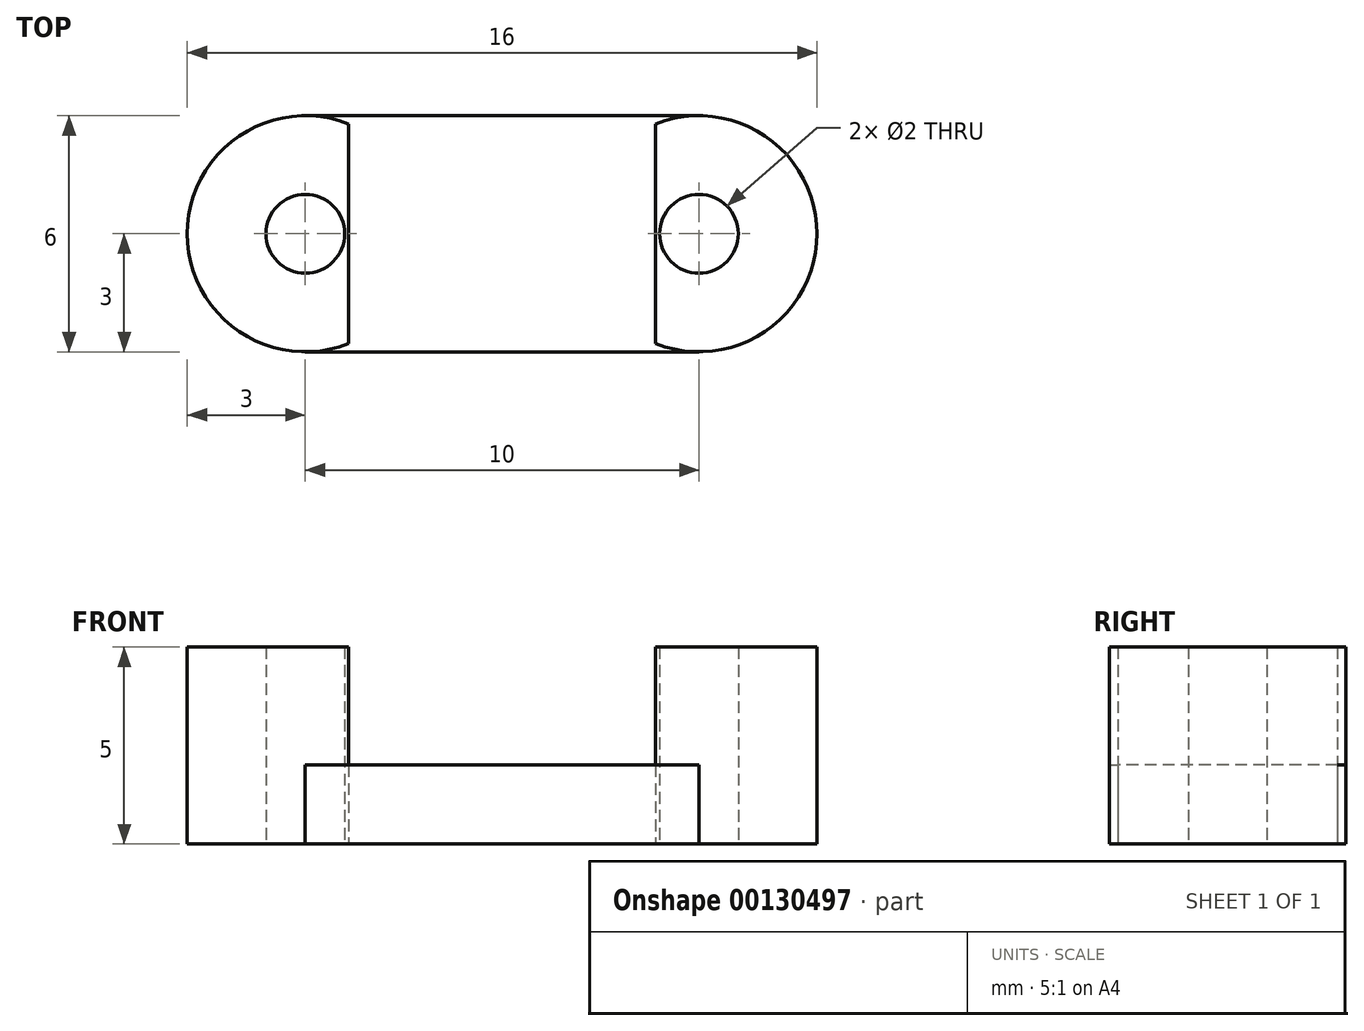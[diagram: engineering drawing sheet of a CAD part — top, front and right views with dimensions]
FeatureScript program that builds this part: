
annotation { "Feature Type Name" : "Feature", "Feature Type Description" : "" }
export const myFeature = defineFeature(function(context is Context, id is Id, definition is map)
    precondition{}
    {
        {
            var Q0;
            Q0=qCreatedBy(makeId("Top.planeOp"),FACE);
            var sketch = newSketch(context, id + "F0", { "sketchPlane" : qUnion([Q0])});
            skCircle(sketch, "E0", {"center": v(0, 0) * mm, "radius": 3 * mm});
            skCircle(sketch, "E1", {"center": v(0, 0) * mm, "radius": 1 * mm});
            skLineSegment(sketch, "E2", {"start": v(1.1, 2.8) * mm, "end": v(1.1, -2.8) * mm});
            skCircle(sketch, "E3", {"center": v(10, 0) * mm, "radius": 3 * mm});
            skCircle(sketch, "E4", {"center": v(10, 0) * mm, "radius": 1 * mm});
            skLineSegment(sketch, "E5", {"start": v(0, 3) * mm, "end": v(10, 3) * mm});
            skLineSegment(sketch, "E6", {"start": v(0, -3) * mm, "end": v(10, -3) * mm});
            skLineSegment(sketch, "E7", {"start": v(5, 3) * mm, "end": v(5, -3) * mm});
            skLineSegment(sketch, "E8.MirrorCS", {"start": v(8.9, 2.8) * mm, "end": v(8.9, -2.8) * mm});
            skSolve(sketch);
        }
        {
            var Q0;
            {var subQ0=sQuery(id+"F0.wireOp",EDGE,"E2");var subQ4=sQuery(id+"F0.wireOp",EDGE,"E0");var subQ8=makeQuery(id+"F0.imprint","INTERSECT",VERTEX,{"disambiguationData":[OD(0.0)],"derivedFrom":[subQ4,subQ0]});Q0=makeQuery(id+"F0.imprint","IMPRINT",FACE,{"disambiguationData":[TD([[makeQuery(id+"F0.imprint","IMPRINT",EDGE,{"disambiguationData":[TD([[subQ8,-1.0]])],"derivedFrom":subQ4}),1.0]])]});}
            var Q1;
            {var subQ4=sQuery(id+"F0.wireOp",EDGE,"E3");var subQ5=makeQuery(id+"F0.imprint","INTERSECT",VERTEX,{"derivedFrom":[subQ4,sQuery(id+"F0.wireOp",EDGE,"E5")]});Q1=makeQuery(id+"F0.imprint","IMPRINT",FACE,{"disambiguationData":[TD([[makeQuery(id+"F0.imprint","IMPRINT",EDGE,{"disambiguationData":[TD([[subQ5,-1.0]])],"derivedFrom":subQ4}),1.0]])]});}
            extrude(context, id + "F1", {"entities" : qUnion([Q0, Q1]), "depth" : 5 * mm});
        }
        {
            var Q0;
            {var subQ0=sQuery(id+"F0.wireOp",EDGE,"E2");var subQ1=sQuery(id+"F0.wireOp",EDGE,"E0");var subQ2=makeQuery(id+"F0.imprint","INTERSECT",VERTEX,{"disambiguationData":[OD(0.0)],"derivedFrom":[subQ1,subQ0]});Q0=makeQuery(id+"F0.imprint","IMPRINT",FACE,{"disambiguationData":[TD([[makeQuery(id+"F0.imprint","IMPRINT",EDGE,{"disambiguationData":[TD([[subQ2,1.0]])],"derivedFrom":subQ1}),1.0]])]});}
            var Q1;
            {var subQ3=sQuery(id+"F0.wireOp",EDGE,"E7");Q1=makeQuery(id+"F0.imprint","IMPRINT",FACE,{"disambiguationData":[TD([[makeQuery(id+"F0.imprint","IMPRINT",EDGE,{"derivedFrom":subQ3}),-1.0]])]});}
            var Q2;
            {var subQ3=sQuery(id+"F0.wireOp",EDGE,"E7");Q2=makeQuery(id+"F0.imprint","IMPRINT",FACE,{"disambiguationData":[TD([[makeQuery(id+"F0.imprint","IMPRINT",EDGE,{"derivedFrom":subQ3}),1.0]])]});}
            var Q3;
            {var subQ0=sQuery(id+"F0.wireOp",EDGE,"E8.MirrorCS");var subQ1=sQuery(id+"F0.wireOp",EDGE,"E3");var subQ2=makeQuery(id+"F0.imprint","INTERSECT",VERTEX,{"disambiguationData":[OD(0.0)],"derivedFrom":[subQ1,subQ0]});Q3=makeQuery(id+"F0.imprint","IMPRINT",FACE,{"disambiguationData":[TD([[makeQuery(id+"F0.imprint","IMPRINT",EDGE,{"disambiguationData":[TD([[subQ2,-1.0]])],"derivedFrom":subQ1}),1.0]])]});}
            extrude(context, id + "F2", {"entities" : qUnion([Q0, Q1, Q2, Q3]), "depth" : 2 * mm});
        }
    });
